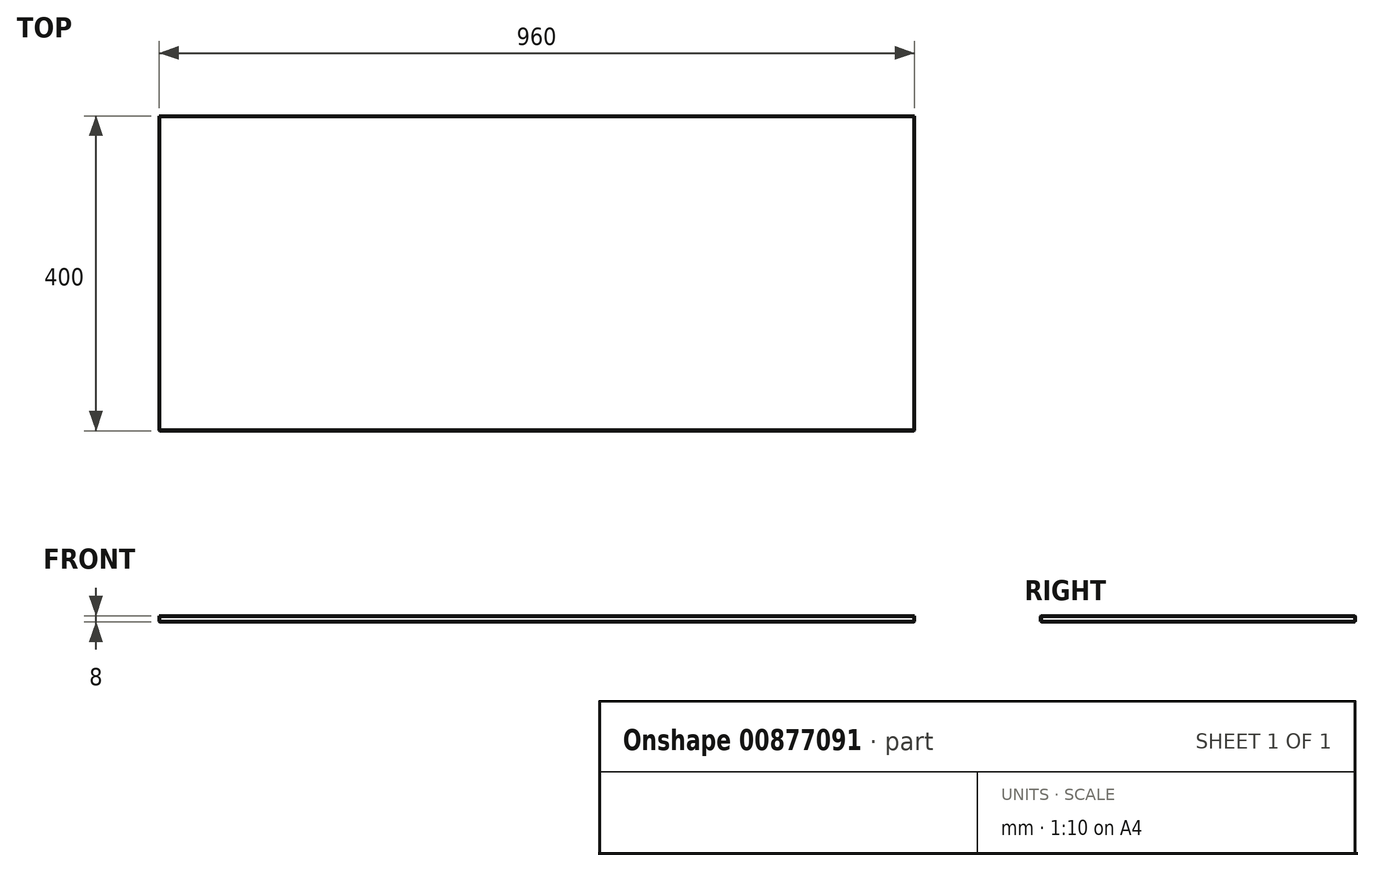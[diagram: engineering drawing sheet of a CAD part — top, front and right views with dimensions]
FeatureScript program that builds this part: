
annotation { "Feature Type Name" : "Feature", "Feature Type Description" : "" }
export const myFeature = defineFeature(function(context is Context, id is Id, definition is map)
    precondition{}
    {
        {
            var Q0;
            Q0=qCreatedBy(makeId("Top.planeOp"),FACE);
            var sketch = newSketch(context, id + "F0", { "sketchPlane" : qUnion([Q0])});
            skLineSegment(sketch, "E0.bottom", {"start": v(-480, 200) * mm, "end": v(480, 200) * mm});
            skLineSegment(sketch, "E0.top", {"start": v(-480, -200) * mm, "end": v(480, -200) * mm});
            skLineSegment(sketch, "E0.left", {"start": v(-480, 200) * mm, "end": v(-480, -200) * mm});
            skLineSegment(sketch, "E0.right", {"start": v(480, 200) * mm, "end": v(480, -200) * mm});
            skPoint(sketch, "E0.middle", {"position": v(0, 0) * mm});
            skSolve(sketch);
        }
        {
            var Q0;
            Q0=makeQuery(id+"F0.imprint","IMPRINT",FACE,{"disambiguationData":[TD([[makeQuery(id+"F0.imprint","IMPRINT",EDGE,{"derivedFrom":sQuery(id+"F0.wireOp",EDGE,"E0.bottom")}),-1.0]])]});
            extrude(context, id + "F1", {"entities" : qUnion([Q0]), "endBound" : BoundingType.SYMMETRIC, "depth" : 8 * mm, "offsetDistance" : 25 * mm});
        }
        {
            var Q0;
            Q0=makeQuery(id+"F1.opExtrude","CAP_EDGE",EDGE,{"disambiguationData":[OSD([sQuery(id+"F0.wireOp",EDGE,"E0.top")])],"isStart":false});
            chamfer(context, id + "F2", {"entities" : qUnion([Q0]), "width" : 1 * mm, "tangentPropagation" : true});
        }
        {
            var Q0;
            Q0=makeQuery(id+"F1.opExtrude","CAP_EDGE",EDGE,{"disambiguationData":[OSD([sQuery(id+"F0.wireOp",EDGE,"E0.right")])],"isStart":false});
            chamfer(context, id + "F3", {"entities" : qUnion([Q0]), "width" : 1 * mm, "tangentPropagation" : true});
        }
        {
            var Q0;
            Q0=makeQuery(id+"F1.opExtrude","CAP_EDGE",EDGE,{"disambiguationData":[OSD([sQuery(id+"F0.wireOp",EDGE,"E0.bottom")])],"isStart":false});
            chamfer(context, id + "F4", {"entities" : qUnion([Q0]), "width" : 1 * mm, "tangentPropagation" : true});
        }
        {
            var Q0;
            Q0=makeQuery(id+"F1.opExtrude","CAP_EDGE",EDGE,{"disambiguationData":[OSD([sQuery(id+"F0.wireOp",EDGE,"E0.top")])],"isStart":true});
            var Q1;
            Q1=makeQuery(id+"F1.opExtrude","CAP_EDGE",EDGE,{"disambiguationData":[OSD([sQuery(id+"F0.wireOp",EDGE,"E0.left")])],"isStart":true});
            var Q2;
            Q2=makeQuery(id+"F1.opExtrude","CAP_EDGE",EDGE,{"disambiguationData":[OSD([sQuery(id+"F0.wireOp",EDGE,"E0.bottom")])],"isStart":true});
            var Q3;
            Q3=makeQuery(id+"F1.opExtrude","CAP_EDGE",EDGE,{"disambiguationData":[OSD([sQuery(id+"F0.wireOp",EDGE,"E0.right")])],"isStart":true});
            chamfer(context, id + "F5", {"entities" : qUnion([Q0, Q1, Q2, Q3]), "width" : 1 * mm, "tangentPropagation" : true});
        }
        {
            var Q0;
            Q0=makeQuery(id+"F1.opExtrude","CAP_EDGE",EDGE,{"disambiguationData":[OSD([sQuery(id+"F0.wireOp",EDGE,"E0.left")])],"isStart":false});
            chamfer(context, id + "F6", {"entities" : qUnion([Q0]), "width" : 1 * mm, "tangentPropagation" : true});
        }
        {
            var Q0;
            Q0=makeQuery(id+"F1.opExtrude","SWEPT_EDGE",EDGE,{"disambiguationData":[OSD([sQuery(id+"F0.wireOp",EDGE,"E0.bottom"),sQuery(id+"F0.wireOp",EDGE,"E0.right")])]});
            var Q1;
            Q1=makeQuery(id+"F1.opExtrude","SWEPT_EDGE",EDGE,{"disambiguationData":[OSD([sQuery(id+"F0.wireOp",EDGE,"E0.top"),sQuery(id+"F0.wireOp",EDGE,"E0.left")])]});
            var Q2;
            Q2=makeQuery(id+"F1.opExtrude","SWEPT_EDGE",EDGE,{"disambiguationData":[OSD([sQuery(id+"F0.wireOp",EDGE,"E0.top"),sQuery(id+"F0.wireOp",EDGE,"E0.right")])]});
            var Q3;
            Q3=makeQuery(id+"F1.opExtrude","SWEPT_EDGE",EDGE,{"disambiguationData":[OSD([sQuery(id+"F0.wireOp",EDGE,"E0.bottom"),sQuery(id+"F0.wireOp",EDGE,"E0.left")])]});
            chamfer(context, id + "F7", {"entities" : qUnion([Q0, Q1, Q2, Q3]), "width" : 1 * mm, "tangentPropagation" : true});
        }
    });
